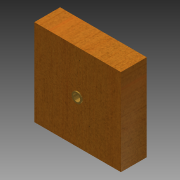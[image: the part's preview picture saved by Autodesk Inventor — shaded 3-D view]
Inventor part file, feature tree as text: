
AUTODESK INVENTOR PART (.ipt)
format: ipt  version: 2014 (Build 180170000, 170)  size: 121,856 bytes
history: native  units: in
note: dims shown in document units (in); Inventor stores cm internally (conversion verified against a paired STEP export)
features: hole x3, extrude x2, sketch x2
ambient origin geometry x8: Origin, YZ Plane, XZ Plane, XY Plane, X Axis, Y Axis, Z Axis, Center Point
bodies: Solid1 (feature_tree)
feature tree (7):
  extrude  "Extrusion1"  Depth=6.0in
  extrude  "Extrusion2"  Depth=0.02in
  hole  "Hole2"  [1 undecoded]
  hole  "Hole3"  [1 undecoded]
  hole  "Hole4"  [1 undecoded]
  sketch  "Sketch1"  dims[d0=6.0in d1=6.0in]
  sketch  "Sketch2"  dims[d2=1.785in d3=0.0in d13=0.5in d14=0.71in d15=3.0in d16=3.0in d17=0.075in d18=0.0in d19=1.0in d20=1.0in d21=0.5in d22=0.75in d23=0.119in d24=0.25in d25=0.5635in d26=0.725in d27=0.0in d48=1.0in d49=1.0in d30=0.48in d31=0.75in d32=0.119in d33=0.25in d34=0.5635in d35=0.305in d36=0.0in d50=1.0in d51=1.0in d41=0.46in d42=0.75in d43=0.119in d44=0.25in d45=0.5635in d46=0.02in d47=0.0in]
note: 3 required parameter values undecoded (feature->parameter linkage not recoverable at this tier; creation-order binding heuristic only, values carry confidence <= 0.55)
